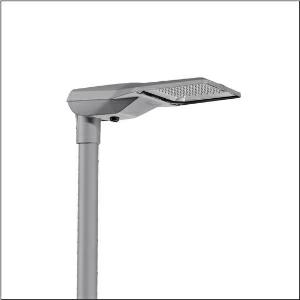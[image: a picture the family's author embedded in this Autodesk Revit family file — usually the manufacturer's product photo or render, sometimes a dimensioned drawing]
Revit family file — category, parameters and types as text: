
# Revit family: streetlight_sl_21_iq_midi___st1_0ab_5xe3m31u08mb_758c
name_source: partatom
category: Lighting Fixtures
units: mm (PartAtom-declared; Revit-internal decimal feet)

## family parameters
Cut with Voids When Loaded = No
Host = Face
Light Source = No
Part Type = Normal
Room Calculation Point = No
Round Connector Dimension = Use Diameter
Shared = No

## types (1)
- --- (1 x LED, 16140 lm, 129.3 W, 3000K)
    Apparent Load = 129 VA
    CIE Flux Codes = 38 73 97 100 100
    Color Rendering = 70
    Color Temperature = 3000K
    Default Elevation = 1800 mm
    Description = Streetlight SL 21 iQ midi, mast luminaire, primary light control with lens, of PMMA, primary optical cover: cover, of toughened safety glass, transparent, light distribution: ST1.0aB, light emission: direct distribution, primary light characteristic: asymmetric, installation type: post-top, side-entry, LED, High Power LED, rated luminous flux: 16.140lm, luminous efficacy: 125lm/W, light colour: 730, colour temperature: 3000K, control: presetting dimming logarithmic, Street-Remote, Auto-Match, Temp-Guard, Lumen-Switch, Night-Set, Smart-Wire, Light-Fading, Desk-Remote (wireless, voltage-free reading and setting of iQ features in the workshop via application-optimized NFC function/RFID function), optimised constant luminous flux control (CLO 2.0), mains connection: 230..240V, AC, 50/60Hz, start of lifetime: 129W, end of service life: 142W, reduction: 56W, luminaire housing, of diecast aluminium, powder-coated, Siteco® metallic grey (DB 702S), corrosivity category C5 mid according to DIN EN ISO 12944, please order mast flange separately, inclination adjustable: 0°, 5°, 10°, 15°, sealing non-destructively replaceable, multi-level sealing system, length: 644mm, width: 335mm, height: 110mm, mast flange for spigot size: 42mm (side-entry): 5XC10008XM4, 60/48mm (side-entry/post-top): 5XC10108XM2, 76/60mm (side-entry/post-top): 5XC10108XM1, Smart Interface below, protection rating (complete): IP66, insulation class (complete): insulation class II (safety insulation), certification: CE, ENEC, ENEC+, VDE, impact resistance: IK09, permissible operating ambient temperature for outdoor applications: -40..+50°C, standard-compliant lighting for roads and squares, packaging unit: 1 piece

Light Distribution: ST1.0aB
    Height = 111 mm
    Lamp = 1 x LED
    Lamp Light Flux = 16140 lm
    Lamp Power = 129.3 W
    Lamp count = 1
    Length = 644 mm
    Luminous efficacy = 125 lm/W
    Manufacturer = Siteco
    ModVariant = No
    Model = 5XE3M31U08MB
    Number of Poles = 1
    OnlyDefault = Yes
    Power Factor = 1
    Product Name = Streetlight SL 21 iQ midi | ST1.0aB
    Product group = mast luminaire | pylon top
    ProductGroupID = 6100
    Protection Class = Protection class II
    Protection Degree = IP 66
    RLX_Detail_Level = 1
    RLX_Emergency_Light_Flux = 0 lm
    RLX_Emergency_Type = 0
    RLX_Emergency_Type_DB = No
    RlxData = <blob elided: 90737 chars, md5=dacfcbab>
    Socket = socket
    Standby Power = 0 W
    System Light Flux = 16141 lm
    System Power = 129 W
    Type Comments = factory setting: luminous flux: 100 % | dim-lin: 254 | 672 mA
    Type Image = l_1004300.jpg
    URL = http://relux.com
    VarID = @adj_042445
    Voltage = 0 V
    Weight = 0.00 kg
    Width = 336 mm

## geometry (parser evidence)
native form markers: Blend x4, Sweep x10
no freeform markers — native parametric forms only
